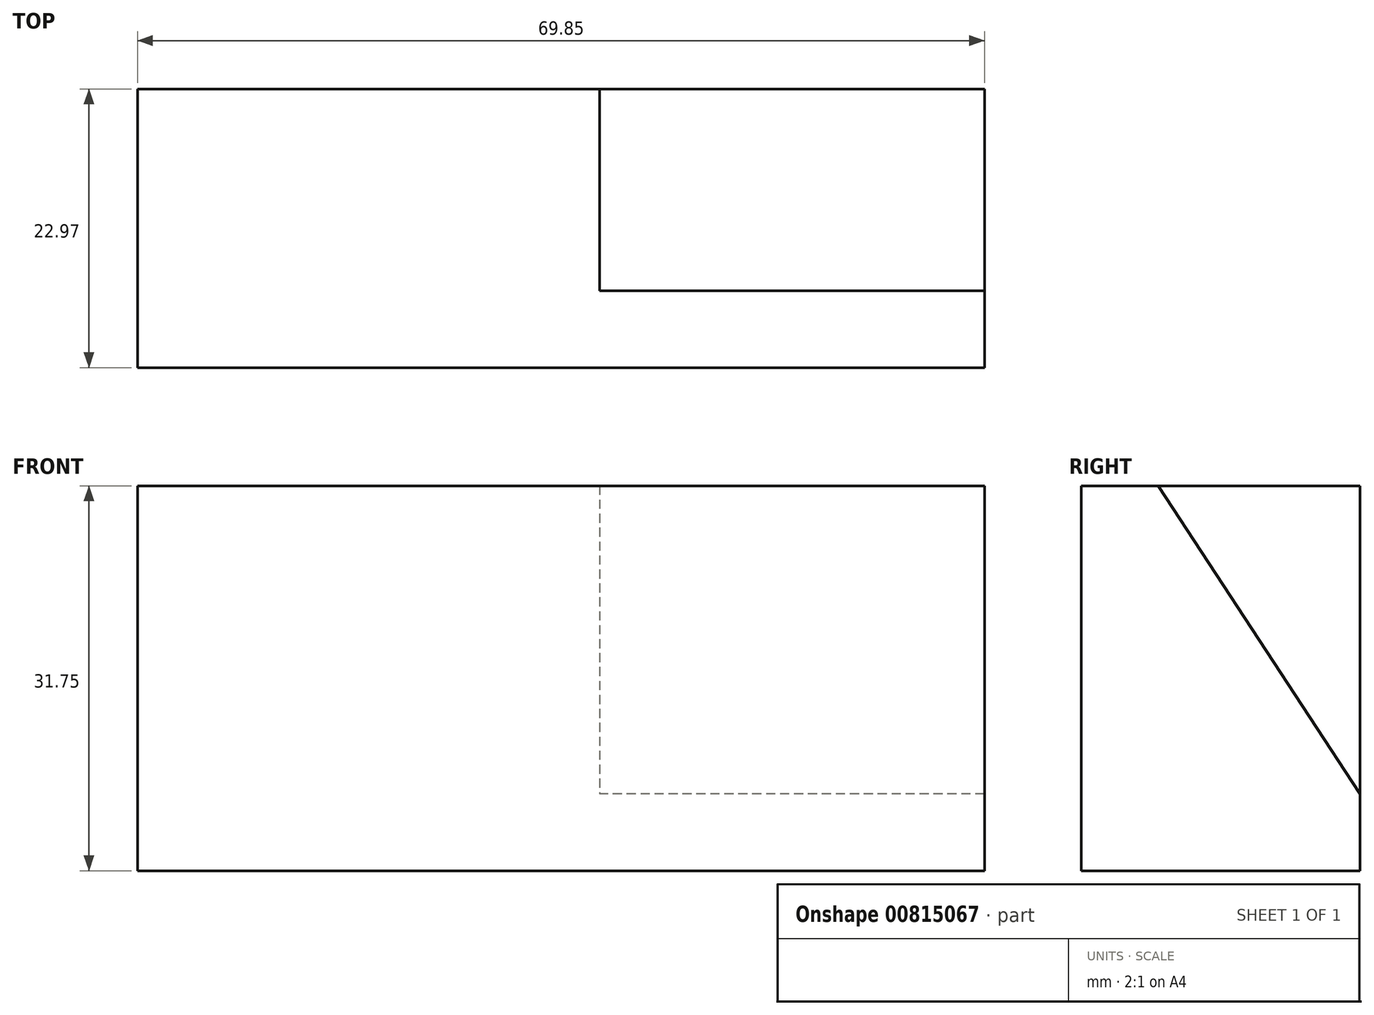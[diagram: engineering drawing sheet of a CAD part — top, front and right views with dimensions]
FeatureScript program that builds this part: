
annotation { "Feature Type Name" : "Feature", "Feature Type Description" : "" }
export const myFeature = defineFeature(function(context is Context, id is Id, definition is map)
    precondition{}
    {
        {
            var Q0;
            Q0=qCreatedBy(makeId("Top.planeOp"),FACE);
            var sketch = newSketch(context, id + "F0", { "sketchPlane" : qUnion([Q0])});
            skLineSegment(sketch, "E0.bottom", {"start": v(0, 5.94) * mm, "end": v(38.1, 5.94) * mm});
            skLineSegment(sketch, "E0.top", {"start": v(0, 28.9) * mm, "end": v(38.1, 28.9) * mm});
            skLineSegment(sketch, "E0.left", {"start": v(0, 5.94) * mm, "end": v(0, 28.9) * mm});
            skLineSegment(sketch, "E0.right", {"start": v(38.1, 5.94) * mm, "end": v(38.1, 28.9) * mm});
            skSolve(sketch);
        }
        {
            var Q0;
            Q0=makeQuery(id+"F0.imprint","IMPRINT",FACE,{"disambiguationData":[TD([[makeQuery(id+"F0.imprint","IMPRINT",EDGE,{"derivedFrom":sQuery(id+"F0.wireOp",EDGE,"E0.bottom")}),1.0]])]});
            extrude(context, id + "F1", {"entities" : qUnion([Q0]), "depth" : 31.75 * mm, "offsetDistance" : 25.4 * mm});
        }
        {
            var Q0;
            Q0=makeQuery(id+"F1.opExtrude","SWEPT_FACE",FACE,{"disambiguationData":[OSD([sQuery(id+"F0.wireOp",EDGE,"E0.right")])]});
            var sketch = newSketch(context, id + "F2", { "sketchPlane" : qUnion([Q0])});
            skLineSegment(sketch, "E1", {"start": v(5.94, 31.75) * mm, "end": v(12.29, 31.75) * mm});
            skLineSegment(sketch, "E2", {"start": v(12.29, 31.75) * mm, "end": v(29.67, 5.18) * mm});
            skLineSegment(sketch, "E3", {"start": v(28.9, 0) * mm, "end": v(28.9, 6.35) * mm});
            skSolve(sketch);
        }
        {
            var Q0;
            Q0 = qSketchRegion(id + "F2", true);
            var Q1;
            {var subQ3=sQuery(id+"F2.wireOp",EDGE,"E1");Q1=makeQuery(id+"F2.imprint","IMPRINT",FACE,{"disambiguationData":[TD([[makeQuery(id+"F2.imprint","IMPRINT",EDGE,{"derivedFrom":subQ3}),-1.0]])]});}
            extrude(context, id + "F3", {"entities" : qUnion([Q0, Q1]), "operationType" : NewBodyOperationType.ADD, "depth" : 31.75 * mm, "offsetDistance" : 25.4 * mm});
        }
    });
